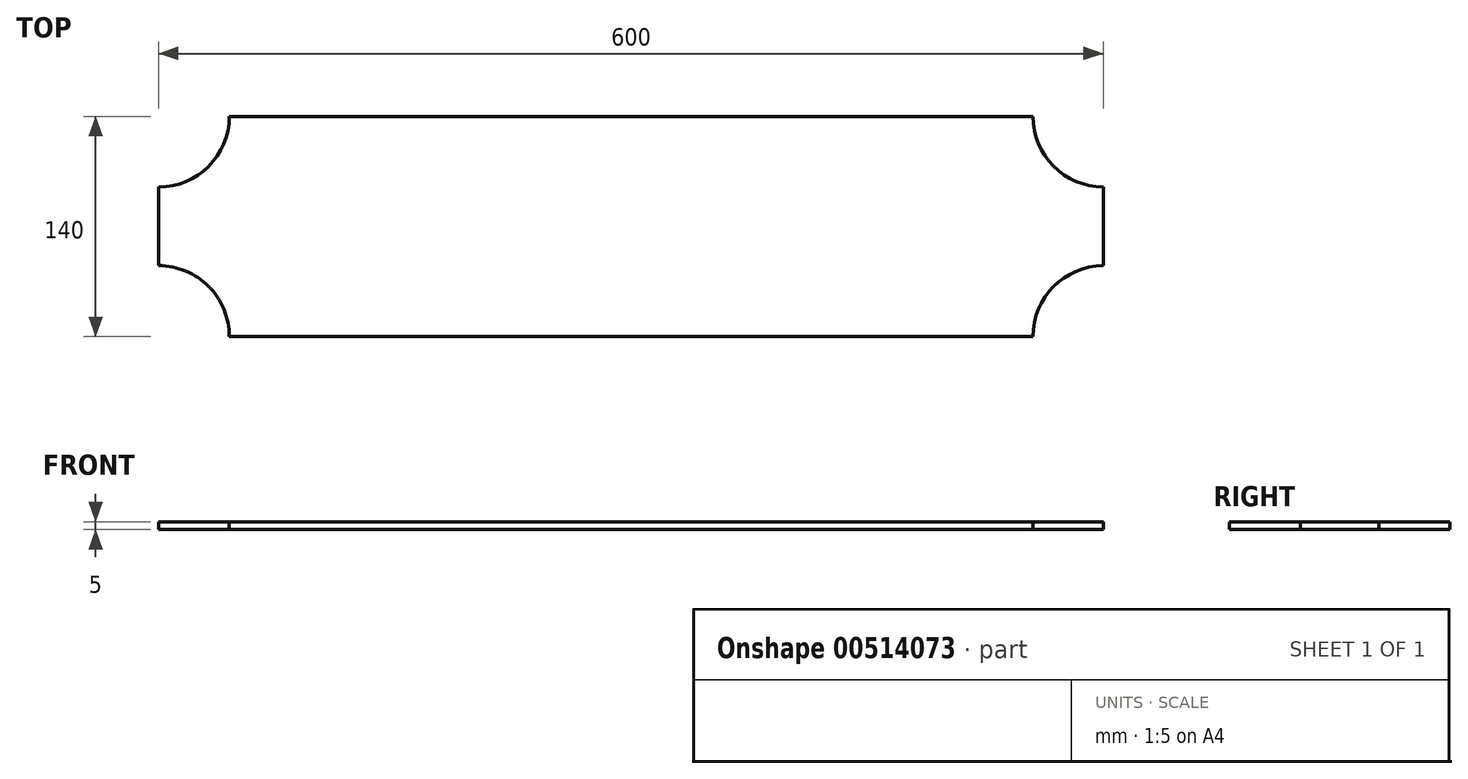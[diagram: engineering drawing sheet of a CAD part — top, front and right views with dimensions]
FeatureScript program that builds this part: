
annotation { "Feature Type Name" : "Feature", "Feature Type Description" : "" }
export const myFeature = defineFeature(function(context is Context, id is Id, definition is map)
    precondition{}
    {
        {
            var Q0;
            Q0=qCreatedBy(makeId("Top.planeOp"),FACE);
            var sketch = newSketch(context, id + "F0", { "sketchPlane" : qUnion([Q0])});
            skLineSegment(sketch, "E0.bottom", {"start": v(-298.21, 77.99) * mm, "end": v(301.79, 77.99) * mm});
            skLineSegment(sketch, "E0.top", {"start": v(-298.21, -62.01) * mm, "end": v(301.79, -62.01) * mm});
            skLineSegment(sketch, "E0.left", {"start": v(-298.21, 77.99) * mm, "end": v(-298.21, -62.01) * mm});
            skLineSegment(sketch, "E0.right", {"start": v(301.79, 77.99) * mm, "end": v(301.79, -62.01) * mm});
            skSolve(sketch);
        }
        {
            var Q0;
            Q0=makeQuery(id+"F0.imprint","IMPRINT",FACE,{"disambiguationData":[TD([[makeQuery(id+"F0.imprint","IMPRINT",EDGE,{"derivedFrom":sQuery(id+"F0.wireOp",EDGE,"E0.bottom")}),-1.0]])]});
            extrude(context, id + "F1", {"entities" : qUnion([Q0]), "depth" : 5 * mm});
        }
        {
            var Q0;
            Q0=qCreatedBy(makeId("Top.planeOp"),FACE);
            var sketch = newSketch(context, id + "F2", { "sketchPlane" : qUnion([Q0])});
            skCircle(sketch, "E1", {"center": v(302.1, -61.88) * mm, "radius": 45 * mm});
            skCircle(sketch, "E2", {"center": v(302.1, 78.04) * mm, "radius": 45 * mm});
            skCircle(sketch, "E3", {"center": v(-298.32, 78.04) * mm, "radius": 45 * mm});
            skCircle(sketch, "E4", {"center": v(-298.32, -61.88) * mm, "radius": 45 * mm});
            skSolve(sketch);
        }
        {
            var Q0;
            Q0=sQuery(id+"F2.wireOp",VERTEX,"E3.center");
            var Q1;
            Q1=sQuery(id+"F2.wireOp",VERTEX,"E4.center");
            var Q2;
            Q2=sQuery(id+"F2.wireOp",VERTEX,"E2.center");
            var Q3;
            Q3=sQuery(id+"F2.wireOp",VERTEX,"E1.center");
            var Q4;
            Q4=makeQuery(id+"F1.opExtrude","SWEPT_BODY",BODY,{"disambiguationData":[OSD([sQuery(id+"F0.wireOp",EDGE,"E0.bottom"),sQuery(id+"F0.wireOp",EDGE,"E0.top"),sQuery(id+"F0.wireOp",EDGE,"E0.left"),sQuery(id+"F0.wireOp",EDGE,"E0.right")])]});
            hole(context, id + "F3", {"style" : HoleStyle.SIMPLE, "endStyle" : HoleEndStyle.THROUGH, "oppositeDirection" : true, "holeDiameter" : 90 * mm, "isTappedThrough" : true, "tappedDepth" : 12.7 * mm, "tapClearance" : 3, "locations" : qUnion([Q0, Q1, Q2, Q3]), "scope" : qUnion([Q4])});
        }
    });
